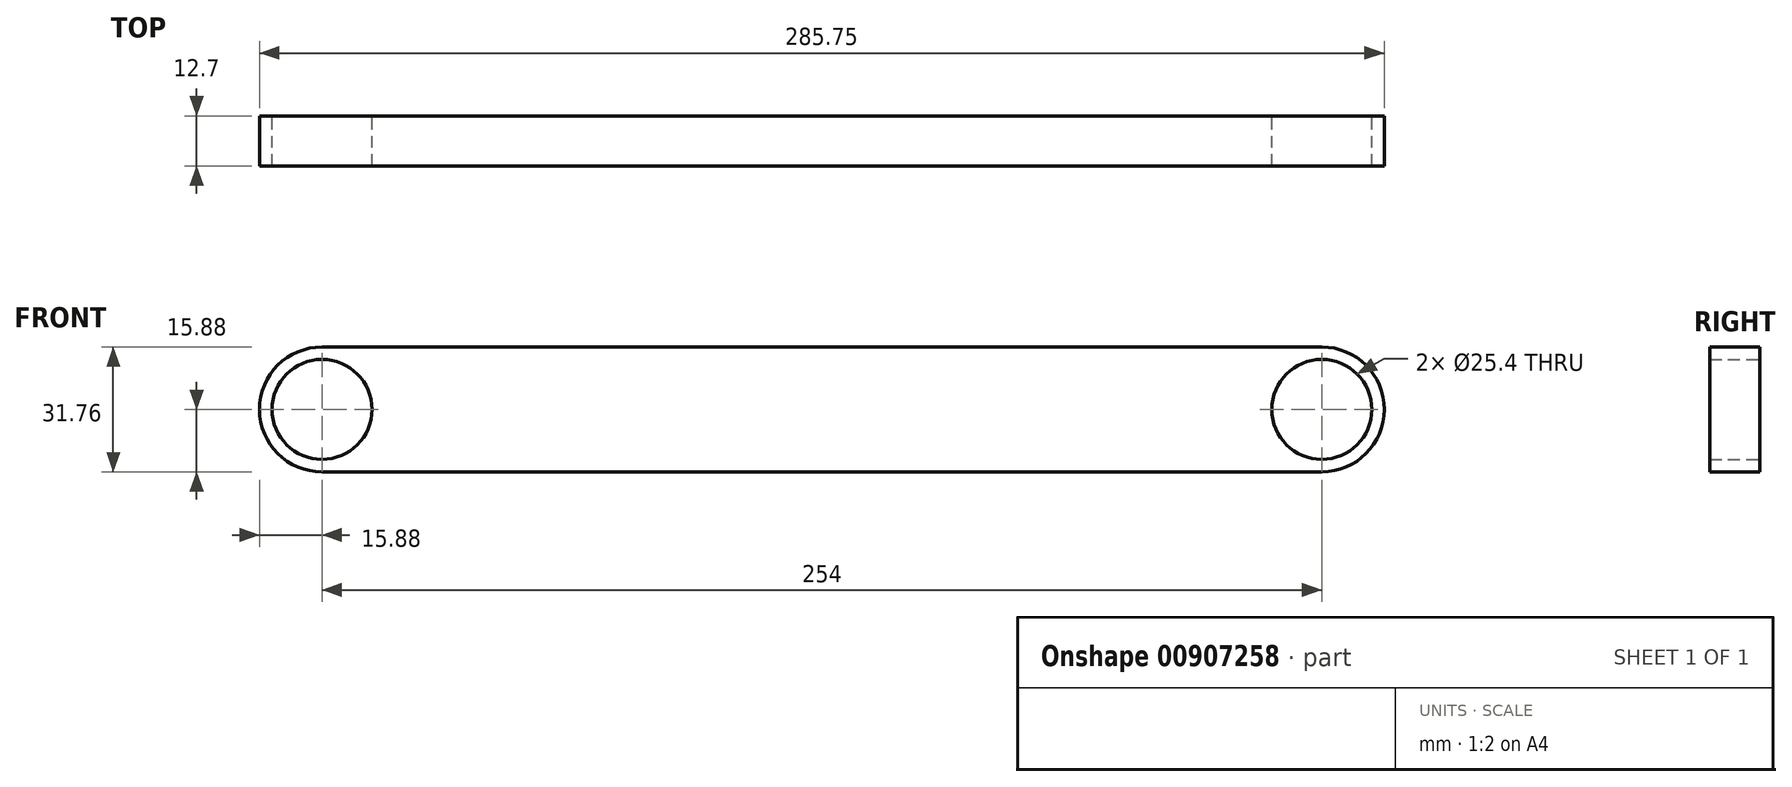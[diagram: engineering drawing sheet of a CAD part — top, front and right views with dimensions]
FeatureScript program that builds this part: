
annotation { "Feature Type Name" : "Feature", "Feature Type Description" : "" }
export const myFeature = defineFeature(function(context is Context, id is Id, definition is map)
    precondition{}
    {
        {
            var Q0;
            Q0=qCreatedBy(makeId("Front.planeOp"),FACE);
            var sketch = newSketch(context, id + "F0", { "sketchPlane" : qUnion([Q0])});
            skLineSegment(sketch, "E0.bottom", {"start": v(127, -15.88) * mm, "end": v(-127, -15.88) * mm});
            skLineSegment(sketch, "E0.top", {"start": v(127, 15.87) * mm, "end": v(-127, 15.87) * mm});
            skPoint(sketch, "E0.middle", {"position": v(0, 0) * mm});
            skArc(sketch, "E1", {"start": v(-127, 15.87) * mm, "mid": v(-142.88, 0) * mm, "end": v(-127, -15.87) * mm});
            skArc(sketch, "E2", {"start": v(127, 15.87) * mm, "mid": v(142.87, 0) * mm, "end": v(127, -15.87) * mm});
            skCircle(sketch, "E3", {"center": v(-127, 0) * mm, "radius": 12.7 * mm});
            skCircle(sketch, "E4", {"center": v(127, 0) * mm, "radius": 12.7 * mm});
            skSolve(sketch);
        }
        {
            var Q0;
            Q0=makeQuery(id+"F0.imprint","IMPRINT",FACE,{"disambiguationData":[TD([[makeQuery(id+"F0.imprint","IMPRINT",EDGE,{"derivedFrom":sQuery(id+"F0.wireOp",EDGE,"E0.bottom")}),-1.0]])]});
            extrude(context, id + "F1", {"entities" : qUnion([Q0]), "depth" : 12.7 * mm, "offsetDistance" : 25.4 * mm});
        }
    });
